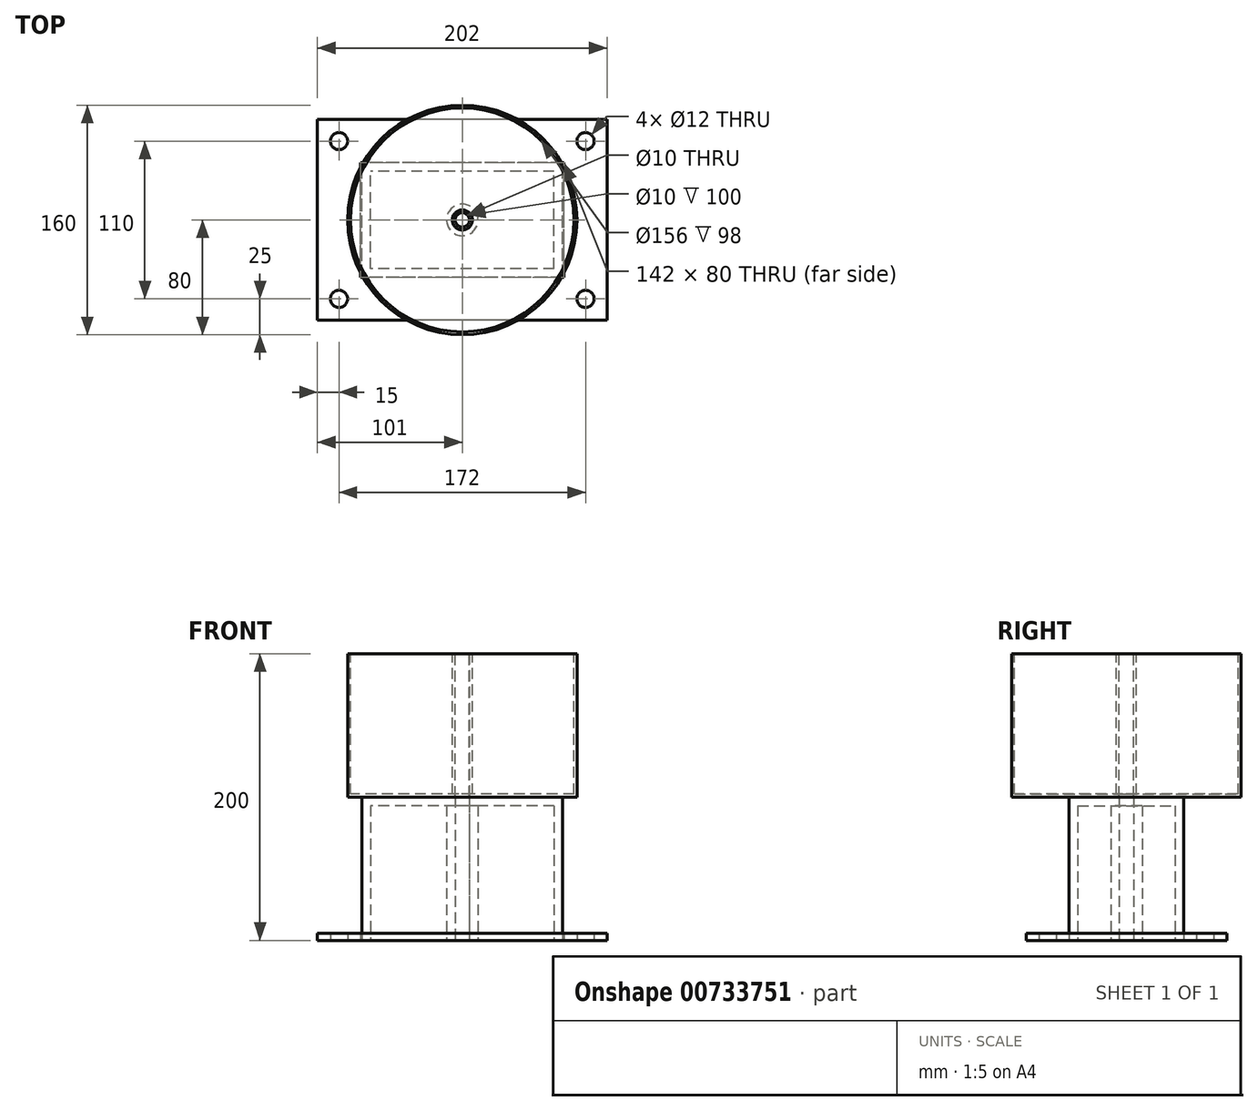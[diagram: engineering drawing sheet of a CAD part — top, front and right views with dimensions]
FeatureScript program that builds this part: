
annotation { "Feature Type Name" : "Feature", "Feature Type Description" : "" }
export const myFeature = defineFeature(function(context is Context, id is Id, definition is map)
    precondition{}
    {
        {
            var Q0;
            Q0=qCreatedBy(makeId("Top.planeOp"),FACE);
            var sketch = newSketch(context, id + "F0", { "sketchPlane" : qUnion([Q0])});
            skLineSegment(sketch, "E0.bottom", {"start": v(101, -70) * mm, "end": v(-101, -70) * mm});
            skLineSegment(sketch, "E0.top", {"start": v(101, 70) * mm, "end": v(-101, 70) * mm});
            skLineSegment(sketch, "E0.left", {"start": v(101, -70) * mm, "end": v(101, 70) * mm});
            skLineSegment(sketch, "E0.right", {"start": v(-101, -70) * mm, "end": v(-101, 70) * mm});
            skPoint(sketch, "E0.middle", {"position": v(0, 0) * mm});
            skCircle(sketch, "E1", {"center": v(-86, 55) * mm, "radius": 6 * mm});
            skCircle(sketch, "E2", {"center": v(-86, -55) * mm, "radius": 6 * mm});
            skCircle(sketch, "E3", {"center": v(86, -55) * mm, "radius": 6 * mm});
            skCircle(sketch, "E4", {"center": v(86, 55) * mm, "radius": 6 * mm});
            skLineSegment(sketch, "E5.bottom", {"start": v(71, -40) * mm, "end": v(-71, -40) * mm});
            skLineSegment(sketch, "E5.top", {"start": v(71, 40) * mm, "end": v(-71, 40) * mm});
            skLineSegment(sketch, "E5.left", {"start": v(71, -40) * mm, "end": v(71, 40) * mm});
            skLineSegment(sketch, "E5.right", {"start": v(-71, -40) * mm, "end": v(-71, 40) * mm});
            skSolve(sketch);
        }
        {
            var Q0;
            Q0=qSketchRegion(id+"F0",true);
            extrude(context, id + "F1", {"entities" : qUnion([Q0]), "depth" : 5 * mm, "offsetDistance" : 25 * mm});
        }
        {
            var Q0;
            Q0=qCreatedBy(makeId("Top.planeOp"),FACE);
            var sketch = newSketch(context, id + "F2", { "sketchPlane" : qUnion([Q0])});
            skLineSegment(sketch, "E6", {"start": v(0, 0) * mm, "end": v(-1.73, -79.98) * mm});
            skLineSegment(sketch, "E7", {"start": v(0, 0) * mm, "end": v(0, 80) * mm});
            skLineSegment(sketch, "E8", {"start": v(0, 0) * mm, "end": v(80, 0) * mm});
            skLineSegment(sketch, "E9", {"start": v(0, 0) * mm, "end": v(-79.98, 1.73) * mm});
            skCircle(sketch, "E10", {"center": v(0, 0) * mm, "radius": 5 * mm});
            skLineSegment(sketch, "E11.bottom", {"start": v(70, -40) * mm, "end": v(-70, -40) * mm});
            skLineSegment(sketch, "E11.top", {"start": v(70, 40) * mm, "end": v(-70, 40) * mm});
            skLineSegment(sketch, "E11.left", {"start": v(70, -40) * mm, "end": v(70, 40) * mm});
            skLineSegment(sketch, "E11.right", {"start": v(-70, -40) * mm, "end": v(-70, 40) * mm});
            skSolve(sketch);
        }
        {
            var Q0;
            {var subQ1=sQuery(id+"F2.wireOp",EDGE,"E7");var subQ3=sQuery(id+"F2.wireOp",EDGE,"E10");var subQ4=makeQuery(id+"F2.imprint","INTERSECT",VERTEX,{"derivedFrom":[subQ1,subQ3]});Q0=makeQuery(id+"F2.imprint","IMPRINT",FACE,{"disambiguationData":[TD([[makeQuery(id+"F2.imprint","IMPRINT",EDGE,{"disambiguationData":[TD([[subQ4,1.0]])],"derivedFrom":subQ3}),1.0]])]});}
            var Q1;
            {var subQ1=sQuery(id+"F2.wireOp",EDGE,"E7");var subQ3=sQuery(id+"F2.wireOp",EDGE,"E10");var subQ4=makeQuery(id+"F2.imprint","INTERSECT",VERTEX,{"derivedFrom":[subQ1,subQ3]});Q1=makeQuery(id+"F2.imprint","IMPRINT",FACE,{"disambiguationData":[TD([[makeQuery(id+"F2.imprint","IMPRINT",EDGE,{"disambiguationData":[TD([[subQ4,-1.0]])],"derivedFrom":subQ3}),1.0]])]});}
            var Q2;
            {var subQ1=sQuery(id+"F2.wireOp",EDGE,"E6");var subQ3=sQuery(id+"F2.wireOp",EDGE,"E10");var subQ4=makeQuery(id+"F2.imprint","INTERSECT",VERTEX,{"derivedFrom":[subQ1,subQ3]});Q2=makeQuery(id+"F2.imprint","IMPRINT",FACE,{"disambiguationData":[TD([[makeQuery(id+"F2.imprint","IMPRINT",EDGE,{"disambiguationData":[TD([[subQ4,1.0]])],"derivedFrom":subQ3}),1.0]])]});}
            var Q3;
            {var subQ1=sQuery(id+"F2.wireOp",EDGE,"E6");var subQ3=sQuery(id+"F2.wireOp",EDGE,"E10");var subQ4=makeQuery(id+"F2.imprint","INTERSECT",VERTEX,{"derivedFrom":[subQ1,subQ3]});Q3=makeQuery(id+"F2.imprint","IMPRINT",FACE,{"disambiguationData":[TD([[makeQuery(id+"F2.imprint","IMPRINT",EDGE,{"disambiguationData":[TD([[subQ4,-1.0]])],"derivedFrom":subQ3}),1.0]])]});}
            extrude(context, id + "F3", {"entities" : qUnion([Q0, Q1, Q2, Q3]), "depth" : 200 * mm, "offsetDistance" : 25 * mm});
        }
        {
            var Q0;
            Q0=makeQuery(id+"F3.opExtrude","CAP_FACE",FACE,{"disambiguationData":[OSD([sQuery(id+"F2.wireOp",EDGE,"E10")])],"isStart":false});
            var sketch = newSketch(context, id + "F4", { "sketchPlane" : qUnion([Q0])});
            skCircle(sketch, "E12", {"center": v(0, 0) * mm, "radius": 80 * mm});
            skLineSegment(sketch, "E13", {"start": v(0, 0) * mm, "end": v(80, 0) * mm});
            skLineSegment(sketch, "E14", {"start": v(0, 0) * mm, "end": v(0, -80) * mm});
            skLineSegment(sketch, "E15", {"start": v(0, 0) * mm, "end": v(-80, 0) * mm});
            skLineSegment(sketch, "E16", {"start": v(0, 0) * mm, "end": v(0, 80) * mm});
            skSolve(sketch);
        }
        {
            var Q0;
            Q0=qSketchRegion(id+"F2",true);
            extrude(context, id + "F5", {"entities" : qUnion([Q0]), "depth" : 100 * mm, "offsetDistance" : 25 * mm});
        }
        {
            var Q0;
            {var subQ0=sQuery(id+"F4.wireOp",EDGE,"E14");var subQ1=sQuery(id+"F4.wireOp",EDGE,"E12");var subQ2=makeQuery(id+"F4.imprint","INTERSECT",VERTEX,{"derivedFrom":[subQ1,subQ0]});Q0=makeQuery(id+"F4.imprint","IMPRINT",FACE,{"disambiguationData":[TD([[makeQuery(id+"F4.imprint","IMPRINT",EDGE,{"disambiguationData":[TD([[subQ2,1.0]])],"derivedFrom":subQ1}),1.0]])]});}
            var Q1;
            {var subQ0=sQuery(id+"F4.wireOp",EDGE,"E15");var subQ1=sQuery(id+"F4.wireOp",EDGE,"E12");var subQ2=makeQuery(id+"F4.imprint","INTERSECT",VERTEX,{"derivedFrom":[subQ1,subQ0]});Q1=makeQuery(id+"F4.imprint","IMPRINT",FACE,{"disambiguationData":[TD([[makeQuery(id+"F4.imprint","IMPRINT",EDGE,{"disambiguationData":[TD([[subQ2,1.0]])],"derivedFrom":subQ1}),1.0]])]});}
            var Q2;
            {var subQ0=sQuery(id+"F4.wireOp",EDGE,"E13");var subQ1=sQuery(id+"F4.wireOp",EDGE,"E12");var subQ2=makeQuery(id+"F4.imprint","INTERSECT",VERTEX,{"derivedFrom":[subQ1,subQ0]});Q2=makeQuery(id+"F4.imprint","IMPRINT",FACE,{"disambiguationData":[TD([[makeQuery(id+"F4.imprint","IMPRINT",EDGE,{"disambiguationData":[TD([[subQ2,-1.0]])],"derivedFrom":subQ1}),1.0]])]});}
            var Q3;
            {var subQ0=sQuery(id+"F4.wireOp",EDGE,"E13");var subQ1=sQuery(id+"F4.wireOp",EDGE,"E12");var subQ2=makeQuery(id+"F4.imprint","INTERSECT",VERTEX,{"derivedFrom":[subQ1,subQ0]});Q3=makeQuery(id+"F4.imprint","IMPRINT",FACE,{"disambiguationData":[TD([[makeQuery(id+"F4.imprint","IMPRINT",EDGE,{"disambiguationData":[TD([[subQ2,1.0]])],"derivedFrom":subQ1}),1.0]])]});}
            extrude(context, id + "F6", {"entities" : qUnion([Q0, Q1, Q2, Q3]), "oppositeDirection" : true, "depth" : 100 * mm, "offsetDistance" : 25 * mm});
        }
        {
            var Q0;
            Q0=makeQuery(id+"F6.opExtrude","CAP_FACE",FACE,{"disambiguationData":[OSD([sQuery(id+"F2.wireOp",EDGE,"E10"),sQuery(id+"F4.wireOp",EDGE,"E12")])],"isStart":true});
            shell(context, id + "F7", {"entities" : qUnion([Q0]), "thickness" : 2 * mm});
        }
        {
            var Q0;
            Q0=makeQuery(id+"F5.opExtrude","CAP_FACE",FACE,{"disambiguationData":[OSD([sQuery(id+"F2.wireOp",EDGE,"E10"),sQuery(id+"F2.wireOp",EDGE,"E11.bottom"),sQuery(id+"F2.wireOp",EDGE,"E11.top"),sQuery(id+"F2.wireOp",EDGE,"E11.left"),sQuery(id+"F2.wireOp",EDGE,"E11.right")])],"isStart":true});
            shell(context, id + "F8", {"entities" : qUnion([Q0]), "thickness" : 6 * mm});
        }
    });
